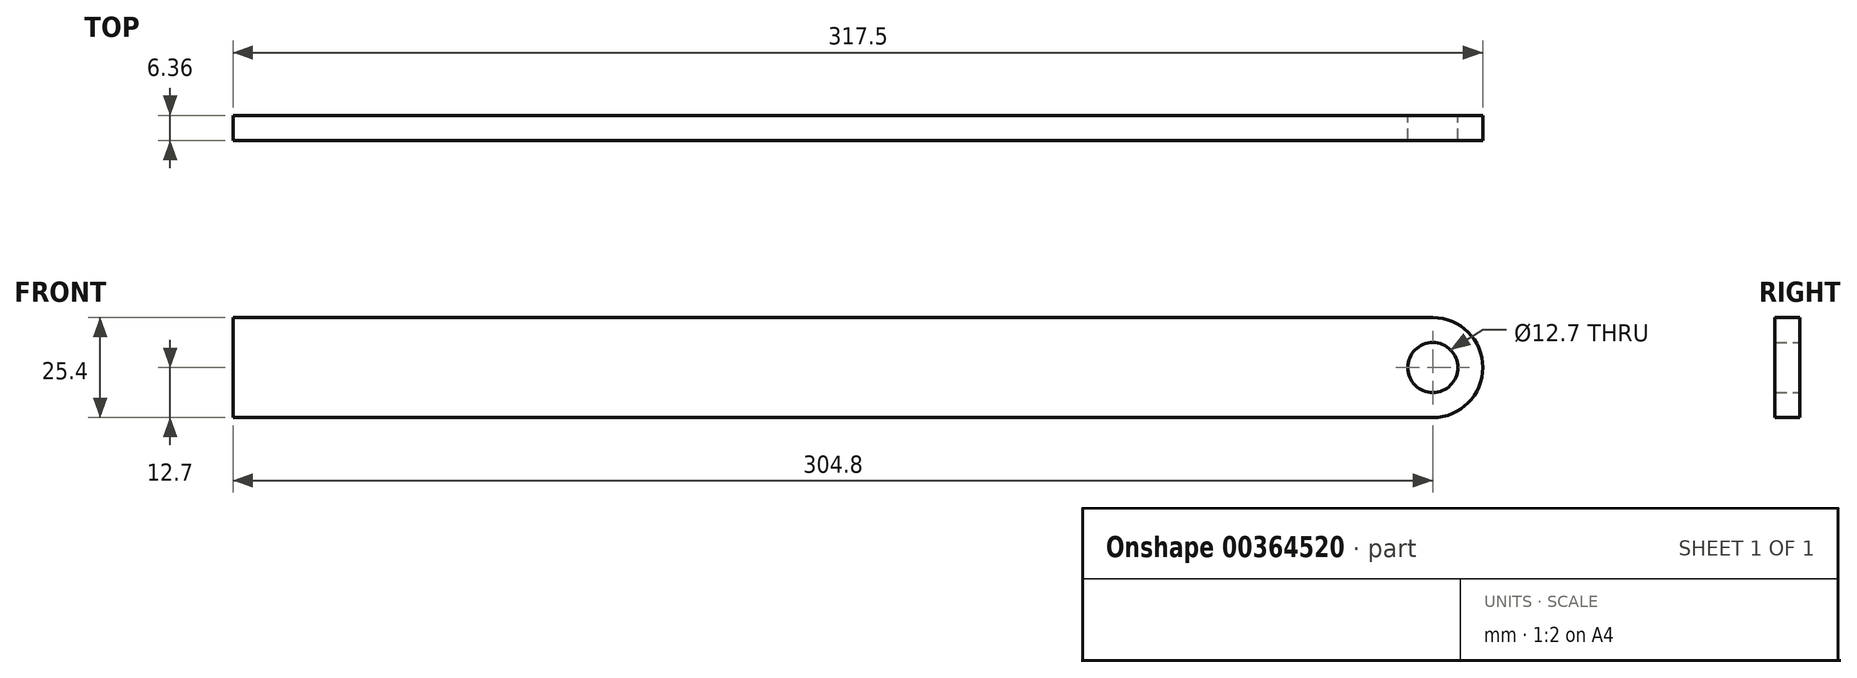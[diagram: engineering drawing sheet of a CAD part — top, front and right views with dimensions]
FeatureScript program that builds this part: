
annotation { "Feature Type Name" : "Feature", "Feature Type Description" : "" }
export const myFeature = defineFeature(function(context is Context, id is Id, definition is map)
    precondition{}
    {
        {
            var Q0;
            Q0=qCreatedBy(makeId("Front.planeOp"),FACE);
            var sketch = newSketch(context, id + "F0", { "sketchPlane" : qUnion([Q0])});
            skLineSegment(sketch, "E0", {"start": v(152.4, 0) * mm, "end": v(-152.4, 0) * mm, "construction": true});
            skArc(sketch, "E1.0.startCap", {"start": v(152.4, 12.7) * mm, "mid": v(165.1, 0) * mm, "end": v(152.4, -12.7) * mm});
            skArc(sketch, "E1.0.endCap", {"start": v(-152.4, -12.7) * mm, "mid": v(-165.1, 0) * mm, "end": v(-152.4, 12.7) * mm, "construction": true});
            skLineSegment(sketch, "E1.0.left", {"start": v(152.4, -12.7) * mm, "end": v(-152.4, -12.7) * mm});
            skLineSegment(sketch, "E1.0.right", {"start": v(152.4, 12.7) * mm, "end": v(-152.4, 12.7) * mm});
            skCircle(sketch, "E2", {"center": v(152.4, 0) * mm, "radius": 6.35 * mm});
            skLineSegment(sketch, "E3", {"start": v(-152.4, 12.7) * mm, "end": v(-152.4, -12.7) * mm});
            skSolve(sketch);
        }
        {
            var Q0;
            Q0 = qSketchRegion(id + "F0", true);
            extrude(context, id + "F1", {"entities" : qUnion([Q0]), "endBound" : BoundingType.SYMMETRIC, "depth" : 6.35 * mm});
        }
    });
